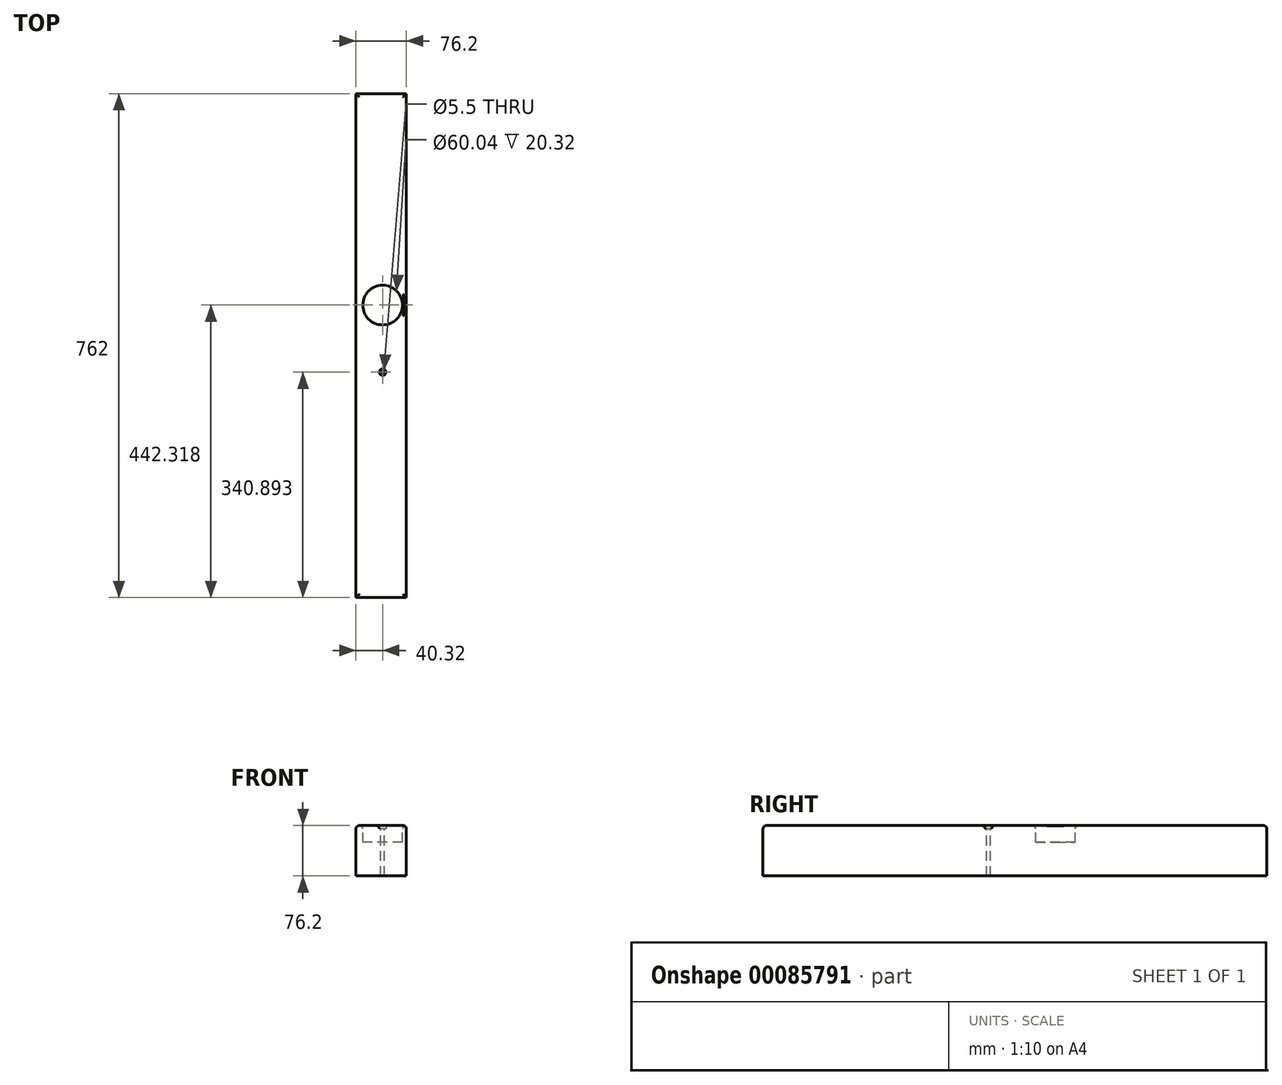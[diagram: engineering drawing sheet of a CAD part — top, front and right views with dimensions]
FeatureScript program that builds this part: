
annotation { "Feature Type Name" : "Feature", "Feature Type Description" : "" }
export const myFeature = defineFeature(function(context is Context, id is Id, definition is map)
    precondition{}
    {
        {
            var Q0;
            Q0=qCreatedBy(makeId("Front.planeOp"),FACE);
            var sketch = newSketch(context, id + "F0", { "sketchPlane" : qUnion([Q0])});
            skLineSegment(sketch, "E0.bottom", {"start": v(-40.32, 51.42) * mm, "end": v(35.88, 51.42) * mm});
            skLineSegment(sketch, "E0.top", {"start": v(-40.32, -24.78) * mm, "end": v(35.88, -24.78) * mm});
            skLineSegment(sketch, "E0.left", {"start": v(-40.32, 51.42) * mm, "end": v(-40.32, -24.78) * mm});
            skLineSegment(sketch, "E0.right", {"start": v(35.88, 51.42) * mm, "end": v(35.88, -24.78) * mm});
            skSolve(sketch);
        }
        {
            var Q0;
            Q0 = qSketchRegion(id + "F0", true);
            extrude(context, id + "F1", {"entities" : qUnion([Q0]), "depth" : 762 * mm});
        }
        {
            var Q0;
            Q0=makeQuery(id+"F1.opExtrude","SWEPT_FACE",FACE,{"disambiguationData":[OSD([sQuery(id+"F0.wireOp",EDGE,"E0.bottom")])]});
            var sketch = newSketch(context, id + "F2", { "sketchPlane" : qUnion([Q0])});
            skCircle(sketch, "E1", {"center": v(0, -421.1) * mm, "radius": 33.62 * mm});
            skSolve(sketch);
        }
        {
            var Q0;
            Q0=sQuery(id+"F2.wireOp",VERTEX,"E1.center");
            var Q1;
            Q1=makeQuery(id+"F1.opExtrude","SWEPT_BODY",BODY,{"disambiguationData":[OSD([sQuery(id+"F0.wireOp",EDGE,"E0.bottom"),sQuery(id+"F0.wireOp",EDGE,"E0.top"),sQuery(id+"F0.wireOp",EDGE,"E0.left"),sQuery(id+"F0.wireOp",EDGE,"E0.right")])]});
            hole(context, id + "F3", {"style" : HoleStyle.C_BORE, "endStyle" : HoleEndStyle.THROUGH, "standardTappedOrClearance" : lookupTablePath({ "standard" : "ISO", "fit" : "Normal", "size" : "M5", "type" : "Clearance" }), "standardBlindInLast" : lookupTablePath({ "fit" : "Standard", "standard" : "ISO", "size" : "M5", "type" : "Clearance" }), "holeDiameter" : 5.5 * mm, "cBoreDiameter" : 9.75 * mm, "cBoreDepth" : 5 * mm, "locations" : qUnion([Q0]), "scope" : qUnion([Q1]), "isTappedThrough" : true});
        }
        {
            var Q0;
            Q0=makeQuery(id+"F1.opExtrude","SWEPT_FACE",FACE,{"disambiguationData":[OSD([sQuery(id+"F0.wireOp",EDGE,"E0.bottom")])]});
            var sketch = newSketch(context, id + "F4", { "sketchPlane" : qUnion([Q0])});
            skCircle(sketch, "E2", {"center": v(0, -319.68) * mm, "radius": 30.02 * mm});
            skSolve(sketch);
        }
        {
            var Q0;
            Q0 = qSketchRegion(id + "F4", true);
            extrude(context, id + "F5", {"entities" : qUnion([Q0]), "operationType" : NewBodyOperationType.REMOVE, "oppositeDirection" : true, "depth" : 25.4 * mm});
        }
        {
            var Q0;
            Q0=makeQuery(id+"F1.opExtrude","SWEPT_FACE",FACE,{"disambiguationData":[OSD([sQuery(id+"F0.wireOp",EDGE,"E0.bottom")])]});
            fillet(context, id + "F6", {"entities" : qUnion([Q0]), "radius" : 5.08 * mm, "tangentPropagation" : true, "allowEdgeOverflow" : false});
        }
    });
